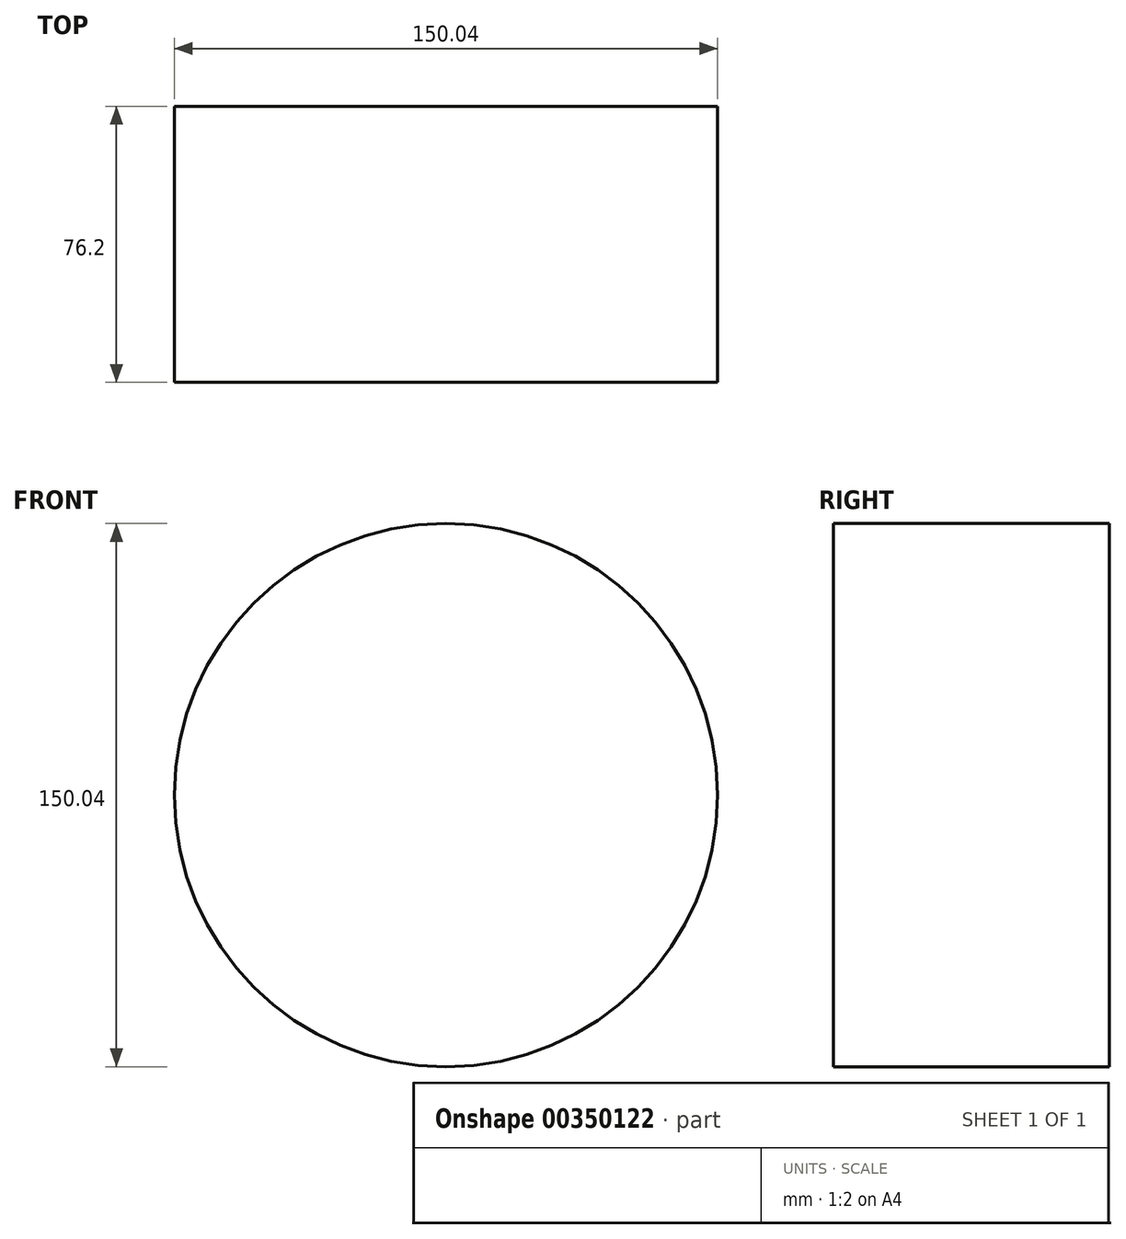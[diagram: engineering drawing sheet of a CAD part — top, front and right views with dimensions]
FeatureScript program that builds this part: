
annotation { "Feature Type Name" : "Feature", "Feature Type Description" : "" }
export const myFeature = defineFeature(function(context is Context, id is Id, definition is map)
    precondition{}
    {
        {
            var Q0;
            Q0=qCreatedBy(makeId("Front.planeOp"),FACE);
            var sketch = newSketch(context, id + "F0", { "sketchPlane" : qUnion([Q0])});
            skCircle(sketch, "E0", {"center": v(0, 0) * mm, "radius": 75.02 * mm});
            skSolve(sketch);
        }
        {
            var Q0;
            Q0=makeQuery(id+"F0.imprint","IMPRINT",FACE,{"disambiguationData":[TD([[makeQuery(id+"F0.imprint","IMPRINT",EDGE,{"derivedFrom":sQuery(id+"F0.wireOp",EDGE,"E0")}),1.0]])]});
            extrude(context, id + "F1", {"entities" : qUnion([Q0]), "depth" : 76.2 * mm});
        }
    });
